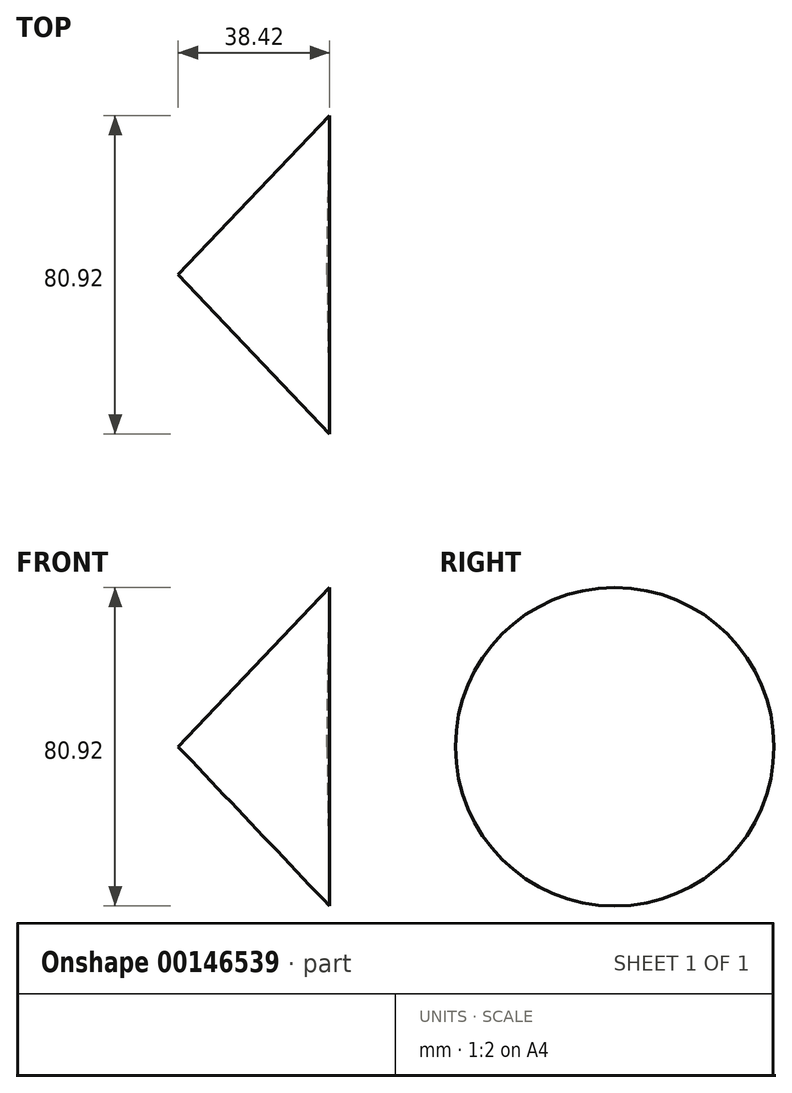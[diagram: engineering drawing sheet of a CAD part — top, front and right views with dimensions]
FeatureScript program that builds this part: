
annotation { "Feature Type Name" : "Feature", "Feature Type Description" : "" }
export const myFeature = defineFeature(function(context is Context, id is Id, definition is map)
    precondition{}
    {
        {
            var Q0;
            Q0=qCreatedBy(makeId("Front.planeOp"),FACE);
            var sketch = newSketch(context, id + "F0", { "sketchPlane" : qUnion([Q0])});
            skLineSegment(sketch, "E0", {"start": v(0, 0) * mm, "end": v(38.42, 40.46) * mm});
            skLineSegment(sketch, "E1", {"start": v(38.42, 40.46) * mm, "end": v(37.8, 0) * mm});
            skLineSegment(sketch, "E2", {"start": v(37.8, 0) * mm, "end": v(0, 0) * mm});
            skSolve(sketch);
        }
        {
            var Q0;
            Q0 = qSketchRegion(id + "F0", true);
            var Q1;
            Q1=sQuery(id+"F0.wireOp",EDGE,"E2");
            revolve(context, id + "F1", {"entities" : qUnion([Q0]), "axis" : qUnion([Q1]), "revolveType" : RevolveType.FULL});
        }
    });
